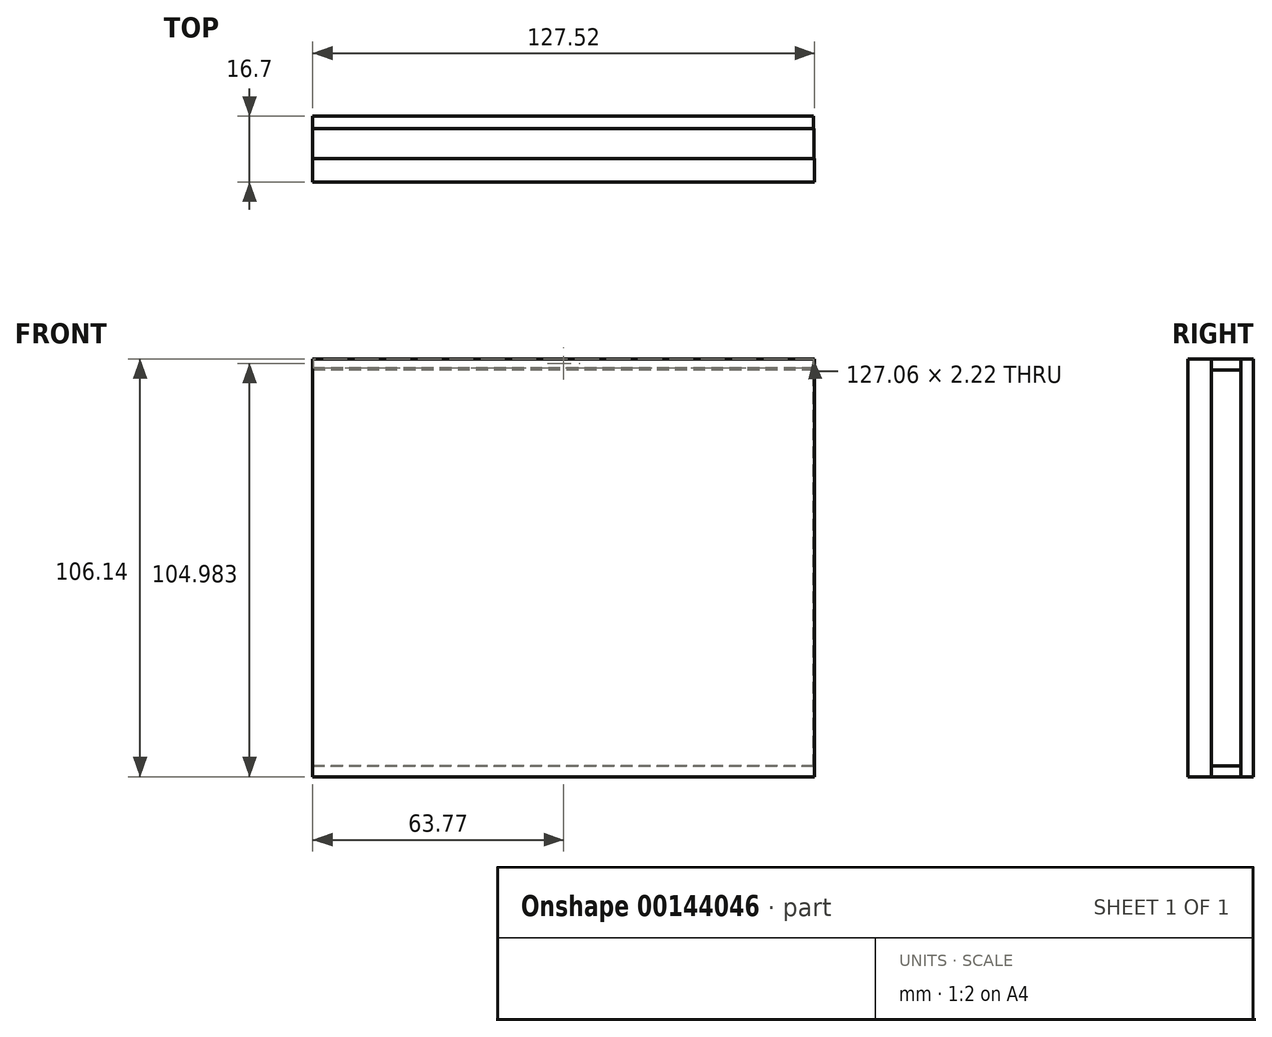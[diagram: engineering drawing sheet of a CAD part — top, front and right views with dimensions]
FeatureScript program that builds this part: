
annotation { "Feature Type Name" : "Feature", "Feature Type Description" : "" }
export const myFeature = defineFeature(function(context is Context, id is Id, definition is map)
    precondition{}
    {
        {
            var Q0;
            Q0=qCreatedBy(makeId("Front.planeOp"),FACE);
            var sketch = newSketch(context, id + "F0", { "sketchPlane" : qUnion([Q0])});
            skLineSegment(sketch, "E0.bottom", {"start": v(63.53, -52.94) * mm, "end": v(-63.53, -52.94) * mm});
            skLineSegment(sketch, "E0.top", {"start": v(63.53, 52.94) * mm, "end": v(-63.53, 52.94) * mm});
            skLineSegment(sketch, "E0.left", {"start": v(63.53, -52.94) * mm, "end": v(63.53, 52.94) * mm});
            skLineSegment(sketch, "E0.right", {"start": v(-63.53, -52.94) * mm, "end": v(-63.53, 52.94) * mm});
            skPoint(sketch, "E0.middle", {"position": v(0, 0) * mm});
            skSolve(sketch);
        }
        {
            var Q0;
            Q0=qSketchRegion(id+"F0",true);
            extrude(context, id + "F1", {"entities" : qUnion([Q0]), "depth" : 10.16 * mm});
        }
        {
            var Q0;
            Q0=qCreatedBy(makeId("Front.planeOp"),FACE);
            var sketch = newSketch(context, id + "F2", { "sketchPlane" : qUnion([Q0])});
            skLineSegment(sketch, "E1.bottom", {"start": v(-54.5, 52.94) * mm, "end": v(54.5, 52.94) * mm});
            skLineSegment(sketch, "E1.top", {"start": v(-54.5, -52.94) * mm, "end": v(54.5, -52.94) * mm});
            skLineSegment(sketch, "E1.left", {"start": v(-54.5, 52.94) * mm, "end": v(-54.5, -52.94) * mm});
            skLineSegment(sketch, "E1.right", {"start": v(54.5, 52.94) * mm, "end": v(54.5, -52.94) * mm});
            skPoint(sketch, "E1.middle", {"position": v(0, 0) * mm});
            skSolve(sketch);
        }
        {
            var Q0;
            Q0=makeQuery(id+"F2.imprint","IMPRINT",FACE,{"disambiguationData":[TD([[makeQuery(id+"F2.imprint","IMPRINT",EDGE,{"derivedFrom":sQuery(id+"F2.wireOp",EDGE,"E1.bottom")}),-1.0]])]});
            extrude(context, id + "F3", {"entities" : qUnion([Q0]), "operationType" : NewBodyOperationType.REMOVE, "depth" : 3.8 * mm});
        }
        {
            var Q0;
            Q0=qCreatedBy(makeId("Top.planeOp"),FACE);
            var sketch = newSketch(context, id + "F4", { "sketchPlane" : qUnion([Q0])});
            skCircle(sketch, "E2", {"center": v(-59.48, -1.57) * mm, "radius": 2.91 * mm});
            skSolve(sketch);
        }
        {
            var Q0;
            Q0=qSketchRegion(id+"F4",true);
            extrude(context, id + "F5", {"entities" : qUnion([Q0]), "operationType" : NewBodyOperationType.REMOVE, "depth" : 62.1 * mm, "hasSecondDirection" : true, "secondDirectionOppositeDirection" : true, "secondDirectionDepth" : 60.44 * mm});
        }
        {
            var Q0;
            Q0=qCreatedBy(makeId("Right.planeOp"),FACE);
            var sketch = newSketch(context, id + "F6", { "sketchPlane" : qUnion([Q0])});
            skLineSegment(sketch, "E3.bottom", {"start": v(-7.77, 50.72) * mm, "end": v(-2.1, 50.72) * mm});
            skLineSegment(sketch, "E3.top", {"start": v(-7.77, -51.05) * mm, "end": v(-2.1, -51.05) * mm});
            skLineSegment(sketch, "E3.left", {"start": v(-7.77, 50.72) * mm, "end": v(-7.77, -51.05) * mm});
            skLineSegment(sketch, "E3.right", {"start": v(-2.1, 50.72) * mm, "end": v(-2.1, -51.05) * mm});
            skSolve(sketch);
        }
        {
            var Q0;
            Q0 = qSketchRegion(id + "F6", true);
            extrude(context, id + "F7", {"entities" : qUnion([Q0]), "operationType" : NewBodyOperationType.REMOVE, "oppositeDirection" : true, "depth" : 87.7 * mm, "hasSecondDirection" : true, "secondDirectionOppositeDirection" : false, "secondDirectionDepth" : 90.01 * mm});
        }
        {
            var Q0;
            Q0=qCreatedBy(makeId("Right.planeOp"),FACE);
            var sketch = newSketch(context, id + "F8", { "sketchPlane" : qUnion([Q0])});
            skLineSegment(sketch, "E4.bottom", {"start": v(-3.31, 51.47) * mm, "end": v(-4.6, 51.47) * mm});
            skLineSegment(sketch, "E4.top", {"start": v(-3.31, -50.55) * mm, "end": v(-4.6, -50.55) * mm});
            skLineSegment(sketch, "E4.left", {"start": v(-3.31, 51.47) * mm, "end": v(-3.31, -50.55) * mm});
            skLineSegment(sketch, "E4.right", {"start": v(-4.6, 51.47) * mm, "end": v(-4.6, -50.55) * mm});
            skSolve(sketch);
        }
        {
            var Q0;
            Q0=qSketchRegion(id+"F8",true);
            extrude(context, id + "F9", {"entities" : qUnion([Q0]), "operationType" : NewBodyOperationType.REMOVE, "depth" : 76.04 * mm, "hasSecondDirection" : true, "secondDirectionOppositeDirection" : true, "secondDirectionDepth" : 72.7 * mm});
        }
        {
            var Q0;
            Q0=qCreatedBy(makeId("Front.planeOp"),FACE);
            var sketch = newSketch(context, id + "F10", { "sketchPlane" : qUnion([Q0])});
            skLineSegment(sketch, "E5.bottom", {"start": v(63.53, 52.94) * mm, "end": v(-63.75, 52.94) * mm});
            skLineSegment(sketch, "E5.top", {"start": v(63.53, -53.15) * mm, "end": v(-63.75, -53.15) * mm});
            skLineSegment(sketch, "E5.left", {"start": v(63.53, 52.94) * mm, "end": v(63.53, -53.15) * mm});
            skLineSegment(sketch, "E5.right", {"start": v(-63.75, 52.94) * mm, "end": v(-63.75, -53.15) * mm});
            skSolve(sketch);
        }
        {
            var Q0;
            Q0 = qSketchRegion(id + "F10", true);
            extrude(context, id + "F11", {"entities" : qUnion([Q0]), "operationType" : NewBodyOperationType.ADD, "oppositeDirection" : true, "depth" : 3.17 * mm});
        }
        {
            var Q0;
            Q0=qCreatedBy(makeId("Front.planeOp"),FACE);
            var sketch = newSketch(context, id + "F12", { "sketchPlane" : qUnion([Q0])});
            skLineSegment(sketch, "E6.bottom", {"start": v(-63.76, 52.95) * mm, "end": v(63.75, 52.95) * mm});
            skLineSegment(sketch, "E6.top", {"start": v(-63.76, -53.15) * mm, "end": v(63.75, -53.15) * mm});
            skLineSegment(sketch, "E6.left", {"start": v(-63.76, 52.95) * mm, "end": v(-63.76, -53.15) * mm});
            skLineSegment(sketch, "E6.right", {"start": v(63.75, 52.95) * mm, "end": v(63.75, -53.15) * mm});
            skSolve(sketch);
        }
        {
            var Q0;
            Q0 = qSketchRegion(id + "F12", true);
            extrude(context, id + "F13", {"entities" : qUnion([Q0]), "operationType" : NewBodyOperationType.ADD, "depth" : 13.53 * mm, "hasSecondDirection" : true, "secondDirectionOppositeDirection" : false, "secondDirectionDepth" : 7.62 * mm});
        }
        {
            var Q0;
            Q0=qCreatedBy(makeId("Right.planeOp"),FACE);
            var sketch = newSketch(context, id + "F14", { "sketchPlane" : qUnion([Q0])});
            skLineSegment(sketch, "E7.bottom", {"start": v(0, 51.68) * mm, "end": v(-7.6, 51.68) * mm});
            skLineSegment(sketch, "E7.top", {"start": v(0, -51.05) * mm, "end": v(-7.6, -51.05) * mm});
            skLineSegment(sketch, "E7.left", {"start": v(0, 51.68) * mm, "end": v(0, -51.05) * mm});
            skLineSegment(sketch, "E7.right", {"start": v(-7.6, 51.68) * mm, "end": v(-7.6, -51.05) * mm});
            skSolve(sketch);
        }
        {
            var Q0;
            Q0 = qSketchRegion(id + "F14", true);
            extrude(context, id + "F15", {"entities" : qUnion([Q0]), "operationType" : NewBodyOperationType.REMOVE, "depth" : 76.4 * mm, "hasSecondDirection" : true, "secondDirectionOppositeDirection" : true, "secondDirectionDepth" : 73.64 * mm});
        }
        {
            var Q0;
            Q0=qCreatedBy(makeId("Right.planeOp"),FACE);
            var sketch = newSketch(context, id + "F16", { "sketchPlane" : qUnion([Q0])});
            skLineSegment(sketch, "E8.bottom", {"start": v(-7.6, 52.99) * mm, "end": v(0, 52.99) * mm});
            skLineSegment(sketch, "E8.top", {"start": v(-7.6, 50.24) * mm, "end": v(0, 50.24) * mm});
            skLineSegment(sketch, "E8.left", {"start": v(-7.6, 52.99) * mm, "end": v(-7.6, 50.24) * mm});
            skLineSegment(sketch, "E8.right", {"start": v(0, 52.99) * mm, "end": v(0, 50.24) * mm});
            skLineSegment(sketch, "E9.bottom", {"start": v(-7.61, -53.13) * mm, "end": v(0, -53.13) * mm});
            skLineSegment(sketch, "E9.top", {"start": v(-7.61, -50.42) * mm, "end": v(0, -50.42) * mm});
            skLineSegment(sketch, "E9.left", {"start": v(-7.61, -53.13) * mm, "end": v(-7.61, -50.42) * mm});
            skLineSegment(sketch, "E9.right", {"start": v(0, -53.13) * mm, "end": v(0, -50.42) * mm});
            skSolve(sketch);
        }
        {
            var Q0;
            Q0 = qSketchRegion(id + "F16", true);
            extrude(context, id + "F17", {"entities" : qUnion([Q0]), "operationType" : NewBodyOperationType.ADD, "depth" : 63.54 * mm, "hasSecondDirection" : true, "secondDirectionOppositeDirection" : true, "secondDirectionDepth" : 63.77 * mm});
        }
    });
